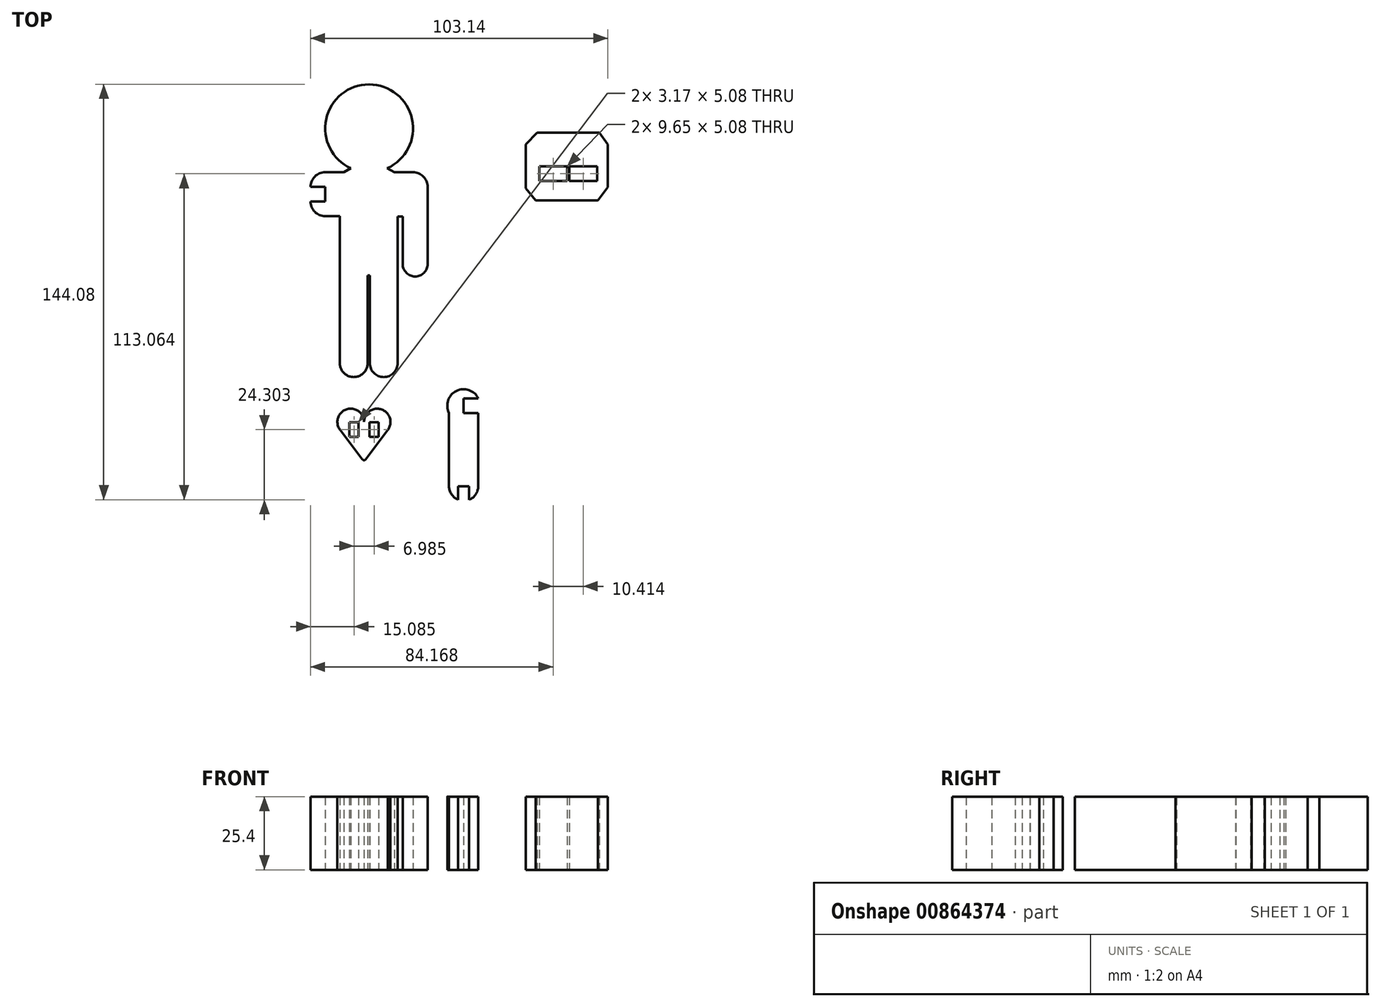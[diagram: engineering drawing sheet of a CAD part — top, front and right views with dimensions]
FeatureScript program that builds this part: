
annotation { "Feature Type Name" : "Feature", "Feature Type Description" : "" }
export const myFeature = defineFeature(function(context is Context, id is Id, definition is map)
    precondition{}
    {
        {
            var Q0;
            Q0=qCreatedBy(makeId("Top.planeOp"),FACE);
            var sketch = newSketch(context, id + "F0", { "sketchPlane" : qUnion([Q0])});
            skPoint(sketch, "E0", {"position": v(-33.27, 29.5) * mm});
            skPoint(sketch, "E1", {"position": v(-33.27, 39.7) * mm});
            skPoint(sketch, "E2", {"position": v(-28.2, 39.7) * mm});
            skPoint(sketch, "E3", {"position": v(-28.2, 12.95) * mm});
            skArc(sketch, "E4", {"start": v(-28.2, 39.7) * mm, "mid": v(-29.68, 43.3) * mm, "end": v(-33.27, 44.79) * mm});
            skPoint(sketch, "E5", {"position": v(-43.43, -21.43) * mm});
            skLineSegment(sketch, "E6", {"start": v(-28.2, 39.7) * mm, "end": v(-28.2, 12.95) * mm});
            skLineSegment(sketch, "E7", {"start": v(-38.6, 12.95) * mm, "end": v(-38.6, -21.43) * mm});
            skArc(sketch, "E8", {"start": v(-38.6, -21.43) * mm, "mid": v(-43.43, -26.26) * mm, "end": v(-48.26, -21.43) * mm});
            skPoint(sketch, "E9", {"position": v(-53.85, -21.43) * mm});
            skArc(sketch, "E10", {"start": v(-49.02, -21.42) * mm, "mid": v(-53.84, -26.26) * mm, "end": v(-58.67, -21.43) * mm});
            skLineSegment(sketch, "E11", {"start": v(-58.67, -21.43) * mm, "end": v(-58.67, 29.55) * mm});
            skPoint(sketch, "E12", {"position": v(-63.75, 29.55) * mm});
            skPoint(sketch, "E13", {"position": v(-63.75, 39.7) * mm});
            skPoint(sketch, "E14", {"position": v(-68.83, 39.7) * mm});
            skArc(sketch, "E15", {"start": v(-68.83, 39.7) * mm, "mid": v(-67.34, 43.3) * mm, "end": v(-63.75, 44.79) * mm});
            skLineSegment(sketch, "E16", {"start": v(-68.83, 39.7) * mm, "end": v(-63.75, 39.7) * mm});
            skLineSegment(sketch, "E17", {"start": v(-63.75, 39.7) * mm, "end": v(-63.75, 34.63) * mm});
            skLineSegment(sketch, "E18", {"start": v(-63.75, 34.63) * mm, "end": v(-68.83, 34.63) * mm});
            skLineSegment(sketch, "E19", {"start": v(-63.75, 44.79) * mm, "end": v(-57.26, 44.79) * mm});
            skPoint(sketch, "E20", {"position": v(-48.51, 44.79) * mm});
            skLineSegment(sketch, "E21", {"start": v(-10.61, -33.62) * mm, "end": v(-15.7, -33.62) * mm});
            skLineSegment(sketch, "E22", {"start": v(-15.7, -33.62) * mm, "end": v(-15.7, -38.7) * mm});
            skLineSegment(sketch, "E23", {"start": v(-15.7, -38.7) * mm, "end": v(-10.61, -38.7) * mm});
            skArc(sketch, "E24", {"start": v(-48.51, 44.79) * mm, "mid": v(-48.51, 44.79) * mm, "end": v(-48.51, 44.79) * mm});
            skPoint(sketch, "E24.second.point", {"position": v(-48.51, 75.27) * mm});
            skPoint(sketch, "E24.third.point", {"position": v(-33.27, 59.8) * mm});
            skPoint(sketch, "E25", {"position": v(-15.7, -36.16) * mm});
            skArc(sketch, "E26", {"start": v(-10.61, -33.62) * mm, "mid": v(-18.23, -31.08) * mm, "end": v(-20.77, -38.7) * mm});
            skLineSegment(sketch, "E27", {"start": v(-20.77, -38.7) * mm, "end": v(-20.77, -64.1) * mm});
            skLineSegment(sketch, "E28", {"start": v(-10.61, -38.7) * mm, "end": v(-10.61, -64.1) * mm});
            skPoint(sketch, "E29", {"position": v(-15.7, -64.1) * mm});
            skLineSegment(sketch, "E30", {"start": v(-15.7, -64.1) * mm, "end": v(-17.6, -64.1) * mm});
            skLineSegment(sketch, "E31", {"start": v(-17.6, -64.1) * mm, "end": v(-15.7, -64.1) * mm});
            skLineSegment(sketch, "E32", {"start": v(-13.79, -64.1) * mm, "end": v(-15.7, -64.1) * mm});
            skLineSegment(sketch, "E33", {"start": v(-17.6, -64.1) * mm, "end": v(-17.6, -69.18) * mm});
            skLineSegment(sketch, "E34", {"start": v(-13.79, -64.1) * mm, "end": v(-13.79, -69.18) * mm});
            skArc(sketch, "E35", {"start": v(-20.77, -64.1) * mm, "mid": v(-19.9, -66.94) * mm, "end": v(-17.6, -68.81) * mm});
            skArc(sketch, "E36", {"start": v(-10.61, -64.1) * mm, "mid": v(-11.48, -66.94) * mm, "end": v(-13.79, -68.81) * mm});
            skPoint(sketch, "E37", {"position": v(-32.51, 12.95) * mm});
            skArc(sketch, "E38", {"start": v(-28.2, 12.95) * mm, "mid": v(-32.51, 8.62) * mm, "end": v(-36.84, 12.95) * mm});
            skLineSegment(sketch, "E39", {"start": v(-38.6, 12.95) * mm, "end": v(-38.6, 29.5) * mm});
            skLineSegment(sketch, "E40", {"start": v(-38.6, 29.5) * mm, "end": v(-36.84, 29.5) * mm});
            skLineSegment(sketch, "E41", {"start": v(-36.84, 29.5) * mm, "end": v(-36.84, 12.95) * mm});
            skLineSegment(sketch, "E42.top", {"start": v(-49.02, 9.05) * mm, "end": v(-48.26, 9.05) * mm});
            skLineSegment(sketch, "E42.left", {"start": v(-49.02, -21.42) * mm, "end": v(-49.02, 9.05) * mm});
            skLineSegment(sketch, "E42.right", {"start": v(-48.26, -21.43) * mm, "end": v(-48.26, 9.05) * mm});
            skLineSegment(sketch, "E43.MirrorCS", {"start": v(34.3, 39.64) * mm, "end": v(30.9, 35.03) * mm});
            skLineSegment(sketch, "E44.MirrorCS", {"start": v(10.51, 41.71) * mm, "end": v(20.16, 41.71) * mm});
            skLineSegment(sketch, "E45", {"start": v(10.51, 46.8) * mm, "end": v(20.16, 46.8) * mm});
            skLineSegment(sketch, "E46", {"start": v(20.16, 46.8) * mm, "end": v(20.16, 41.71) * mm});
            skLineSegment(sketch, "E47", {"start": v(10.51, 46.8) * mm, "end": v(10.51, 41.71) * mm});
            skLineSegment(sketch, "E48", {"start": v(34.3, 54.4) * mm, "end": v(34.3, 49.15) * mm});
            skLineSegment(sketch, "E49.MirrorCS", {"start": v(5.9, 39.16) * mm, "end": v(9.3, 35.03) * mm});
            skLineSegment(sketch, "E50.MirrorCS", {"start": v(34.3, 54.4) * mm, "end": v(31.34, 58.53) * mm});
            skLineSegment(sketch, "E51.MirrorCS", {"start": v(5.9, 54.4) * mm, "end": v(9.75, 58.53) * mm});
            skLineSegment(sketch, "E52.trimOffspring", {"start": v(34.3, 49.15) * mm, "end": v(34.3, 39.64) * mm});
            skLineSegment(sketch, "E53.MirrorCS", {"start": v(5.9, 54.4) * mm, "end": v(5.9, 49.17) * mm});
            skLineSegment(sketch, "E54.MirrorCS", {"start": v(5.9, 48.67) * mm, "end": v(5.9, 39.16) * mm});
            skLineSegment(sketch, "E55", {"start": v(9.75, 58.53) * mm, "end": v(13.5, 58.53) * mm});
            skLineSegment(sketch, "E56", {"start": v(30.9, 35.03) * mm, "end": v(14.22, 35.03) * mm});
            skLineSegment(sketch, "E57.trimOffspring", {"start": v(13.5, 58.53) * mm, "end": v(31.34, 58.53) * mm});
            skLineSegment(sketch, "E58.trimOffspring", {"start": v(13.64, 35.03) * mm, "end": v(9.3, 35.03) * mm});
            skLineSegment(sketch, "E59", {"start": v(5.9, 49.17) * mm, "end": v(5.9, 48.67) * mm});
            skLineSegment(sketch, "E60", {"start": v(13.64, 35.03) * mm, "end": v(14.22, 35.03) * mm});
            skLineSegment(sketch, "E61.MirrorCS", {"start": v(20.93, 41.71) * mm, "end": v(30.58, 41.71) * mm});
            skLineSegment(sketch, "E62", {"start": v(20.93, 46.8) * mm, "end": v(30.58, 46.8) * mm});
            skLineSegment(sketch, "E63", {"start": v(30.58, 46.8) * mm, "end": v(30.58, 41.71) * mm});
            skLineSegment(sketch, "E64", {"start": v(20.93, 46.8) * mm, "end": v(20.93, 41.71) * mm});
            skPoint(sketch, "E65", {"position": v(20.54, 58.53) * mm});
            skLineSegment(sketch, "E66", {"start": v(20.54, 46.8) * mm, "end": v(20.54, 46.78) * mm});
            skPoint(sketch, "E67", {"position": v(20.54, 46.8) * mm});
            skPoint(sketch, "E67.positionSnap0", {"position": v(20.54, 46.78) * mm});
            skPoint(sketch, "E68", {"position": v(20.54, 41.71) * mm});
            skPoint(sketch, "E69.trimOffspring.end.orphan", {"position": v(20.54, 35.03) * mm});
            skLineSegment(sketch, "E70", {"start": v(-58.67, 29.55) * mm, "end": v(-63.75, 29.55) * mm});
            skArc(sketch, "E71", {"start": v(-63.75, 29.55) * mm, "mid": v(-67.34, 31.04) * mm, "end": v(-68.83, 34.63) * mm});
            skPoint(sketch, "E72.orphan", {"position": v(-68.83, 34.63) * mm});
            skLineSegment(sketch, "E73", {"start": v(-57.26, 44.79) * mm, "end": v(-54.78, 46.14) * mm});
            skLineSegment(sketch, "E74.MirrorCS", {"start": v(-39.76, 44.79) * mm, "end": v(-42.24, 46.14) * mm});
            skLineSegment(sketch, "E75.trimOffspring", {"start": v(-48.51, 44.79) * mm, "end": v(-48.51, 44.79) * mm});
            skArc(sketch, "E76.trimOffspring", {"start": v(-42.24, 46.14) * mm, "mid": v(-48.5, 75.27) * mm, "end": v(-54.78, 46.14) * mm});
            skLineSegment(sketch, "E77.trimOffspring", {"start": v(-39.76, 44.79) * mm, "end": v(-33.27, 44.79) * mm});
            skSolve(sketch);
        }
        {
            var Q0;
            Q0=qCreatedBy(makeId("Top.planeOp"),FACE);
            var sketch = newSketch(context, id + "F1", { "sketchPlane" : qUnion([Q0])});
            skPoint(sketch, "E78", {"position": v(-59.5, -41.84) * mm});
            skPoint(sketch, "E79", {"position": v(-41.08, -41.84) * mm});
            skPoint(sketch, "E80", {"position": v(-50.25, -53.77) * mm});
            skPoint(sketch, "E81", {"position": v(-54.88, -41.84) * mm});
            skPoint(sketch, "E82", {"position": v(-45.67, -41.84) * mm});
            skArc(sketch, "E83", {"start": v(-59.5, -41.84) * mm, "mid": v(-54.88, -37.22) * mm, "end": v(-50.25, -41.84) * mm});
            skArc(sketch, "E84", {"start": v(-50.25, -41.84) * mm, "mid": v(-45.67, -37.25) * mm, "end": v(-41.08, -41.84) * mm});
            skArc(sketch, "E85", {"start": v(-50.25, -41.84) * mm, "mid": v(-56.35, -37.46) * mm, "end": v(-58.56, -44.63) * mm});
            skArc(sketch, "E86", {"start": v(-42.02, -44.63) * mm, "mid": v(-44.2, -37.5) * mm, "end": v(-50.25, -41.84) * mm});
            skLineSegment(sketch, "E87", {"start": v(-58.56, -44.63) * mm, "end": v(-50.86, -54.8) * mm});
            skLineSegment(sketch, "E88", {"start": v(-49.65, -54.8) * mm, "end": v(-42.02, -44.63) * mm});
            skPoint(sketch, "E89.visualSharp", {"position": v(-50.25, -55.6) * mm});
            skArc(sketch, "E89.filletArc", {"start": v(-50.86, -54.8) * mm, "mid": v(-50.25, -55.1) * mm, "end": v(-49.65, -54.8) * mm});
            skLineSegment(sketch, "E90", {"start": v(-55.33, -41.97) * mm, "end": v(-52.16, -41.97) * mm});
            skPoint(sketch, "E91", {"position": v(-52.16, -41.97) * mm});
            skPoint(sketch, "E92", {"position": v(-55.33, -41.97) * mm});
            skPoint(sketch, "E93", {"position": v(-48.35, -41.97) * mm});
            skPoint(sketch, "E94", {"position": v(-50.25, -41.97) * mm});
            skLineSegment(sketch, "E95.left", {"start": v(-52.16, -41.97) * mm, "end": v(-52.16, -47.05) * mm});
            skLineSegment(sketch, "E95.right", {"start": v(-48.35, -41.97) * mm, "end": v(-48.35, -47.05) * mm});
            skLineSegment(sketch, "E96.top", {"start": v(-55.33, -47.05) * mm, "end": v(-52.16, -47.05) * mm});
            skLineSegment(sketch, "E96.left", {"start": v(-55.33, -41.97) * mm, "end": v(-55.33, -47.05) * mm});
            skLineSegment(sketch, "E96.right", {"start": v(-45.17, -41.97) * mm, "end": v(-45.17, -47.05) * mm});
            skLineSegment(sketch, "E97.trimOffspring", {"start": v(-48.35, -41.97) * mm, "end": v(-45.17, -41.97) * mm});
            skLineSegment(sketch, "E98.trimOffspring", {"start": v(-48.35, -47.05) * mm, "end": v(-45.17, -47.05) * mm});
            skSolve(sketch);
        }
        {
            var Q0;
            {var subQ1=sQuery(id+"F0.wireOp",EDGE,"E4");Q0=makeQuery(id+"F0.imprint","IMPRINT",FACE,{"disambiguationData":[TD([[makeQuery(id+"F0.imprint","IMPRINT",EDGE,{"derivedFrom":subQ1}),1.0]])]});}
            var sketch = newSketch(context, id + "F2", { "sketchPlane" : qUnion([Q0])});
            skSolve(sketch);
        }
        {
            var Q0;
            Q0=makeQuery(id+"F0.imprint","IMPRINT",FACE,{"disambiguationData":[TD([[makeQuery(id+"F0.imprint","IMPRINT",EDGE,{"derivedFrom":sQuery(id+"F0.wireOp",EDGE,"E4")}),1.0]])]});
            var Q1;
            Q1=makeQuery(id+"F0.imprint","IMPRINT",FACE,{"disambiguationData":[TD([[makeQuery(id+"F0.imprint","IMPRINT",EDGE,{"derivedFrom":sQuery(id+"F0.wireOp",EDGE,"E21")}),-1.0]])]});
            var Q2;
            Q2=makeQuery(id+"F0.imprint","IMPRINT",FACE,{"disambiguationData":[TD([[makeQuery(id+"F0.imprint","IMPRINT",EDGE,{"derivedFrom":sQuery(id+"F0.wireOp",EDGE,"E43.MirrorCS")}),-1.0]])]});
            var Q3;
            Q3=makeQuery(id+"F2.imprint","IMPRINT",FACE,{"disambiguationData":[TD([[makeQuery(id+"F2.imprint","IMPRINT",EDGE,{"derivedFrom":makeQuery(id+"F0.imprint","IMPRINT",EDGE,{"derivedFrom":sQuery(id+"F0.wireOp",EDGE,"E4")})}),1.0]])]});
            var Q4;
            {var subQ3=sQuery(id+"F1.wireOp",EDGE,"E87");Q4=makeQuery(id+"F1.imprint","IMPRINT",FACE,{"disambiguationData":[TD([[makeQuery(id+"F1.imprint","IMPRINT",EDGE,{"derivedFrom":subQ3}),1.0]])]});}
            extrude(context, id + "F3", {"entities" : qUnion([Q0, Q1, Q2, Q3, Q4]), "depth" : 25.4 * mm, "offsetDistance" : 25.4 * mm});
        }
    });
